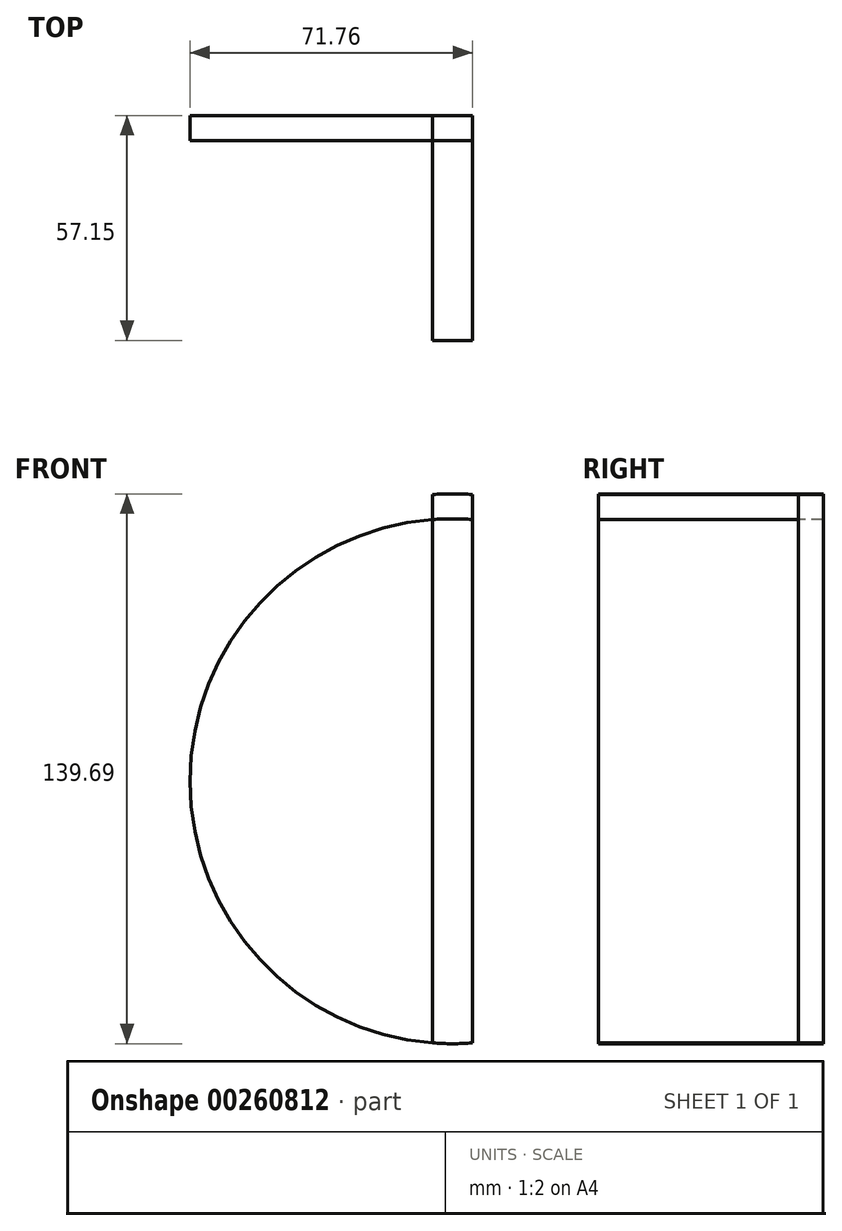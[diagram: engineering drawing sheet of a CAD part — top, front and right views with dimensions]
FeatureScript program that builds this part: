
annotation { "Feature Type Name" : "Feature", "Feature Type Description" : "" }
export const myFeature = defineFeature(function(context is Context, id is Id, definition is map)
    precondition{}
    {
        {
            var Q0;
            Q0=qCreatedBy(makeId("Front.planeOp"),FACE);
            var sketch = newSketch(context, id + "F0", { "sketchPlane" : qUnion([Q0])});
            skCircle(sketch, "E0", {"center": v(0, 0) * mm, "radius": 73.03 * mm});
            skPoint(sketch, "E1", {"position": v(-5.08, 0) * mm});
            skPoint(sketch, "E2.MirrorP", {"position": v(5.08, 0) * mm});
            skCircle(sketch, "E3", {"center": v(0, 0) * mm, "radius": 66.68 * mm});
            skLineSegment(sketch, "E4", {"start": v(-5.08, 0) * mm, "end": v(-5.08, 72.85) * mm});
            skLineSegment(sketch, "E5", {"start": v(-5.08, 72.85) * mm, "end": v(-5.08, -66.48) * mm});
            skLineSegment(sketch, "E6.MirrorCS", {"start": v(5.08, 72.85) * mm, "end": v(5.08, -66.48) * mm});
            skSolve(sketch);
        }
        {
            var Q0;
            {var subQ4=sQuery(id+"F0.wireOp",EDGE,"E5");var subQ7=sQuery(id+"F0.wireOp",EDGE,"E0");var subQ8=makeQuery(id+"F0.imprint","INTERSECT",VERTEX,{"derivedFrom":[subQ7,subQ4]});Q0=makeQuery(id+"F0.imprint","IMPRINT",FACE,{"disambiguationData":[TD([[makeQuery(id+"F0.imprint","IMPRINT",EDGE,{"disambiguationData":[TD([[subQ8,-1.0]])],"derivedFrom":subQ7}),1.0]])]});}
            var Q1;
            {var subQ0=sQuery(id+"F0.wireOp",EDGE,"E6.MirrorCS");var subQ1=sQuery(id+"F0.wireOp",EDGE,"E3");var subQ2=makeQuery(id+"F0.imprint","INTERSECT",VERTEX,{"disambiguationData":[OD(0.0)],"derivedFrom":[subQ1,subQ0]});Q1=makeQuery(id+"F0.imprint","IMPRINT",FACE,{"disambiguationData":[TD([[makeQuery(id+"F0.imprint","IMPRINT",EDGE,{"disambiguationData":[TD([[subQ2,-1.0]])],"derivedFrom":subQ1}),1.0]])]});}
            var Q2;
            {var subQ0=sQuery(id+"F0.wireOp",EDGE,"E5");var subQ1=sQuery(id+"F0.wireOp",EDGE,"E0");var subQ2=makeQuery(id+"F0.imprint","INTERSECT",VERTEX,{"derivedFrom":[subQ1,subQ0]});Q2=makeQuery(id+"F0.imprint","IMPRINT",FACE,{"disambiguationData":[TD([[makeQuery(id+"F0.imprint","IMPRINT",EDGE,{"disambiguationData":[TD([[subQ2,1.0]])],"derivedFrom":subQ1}),1.0]])]});}
            var Q3;
            {var subQ0=sQuery(id+"F0.wireOp",EDGE,"E5");var subQ4=makeQuery(id+"F0.imprint","IMPRINT",VERTEX,{"derivedFrom":subQ0});Q3=makeQuery(id+"F0.imprint","IMPRINT",FACE,{"disambiguationData":[TD([[makeQuery(id+"F0.imprint","IMPRINT",EDGE,{"disambiguationData":[TD([[subQ4,1.0]])],"derivedFrom":subQ0}),-1.0]])]});}
            var Q4;
            {var subQ0=sQuery(id+"F0.wireOp",EDGE,"E5");var subQ3=makeQuery(id+"F0.imprint","IMPRINT",VERTEX,{"derivedFrom":subQ0});Q4=makeQuery(id+"F0.imprint","IMPRINT",FACE,{"disambiguationData":[TD([[makeQuery(id+"F0.imprint","IMPRINT",EDGE,{"disambiguationData":[TD([[subQ3,1.0]])],"derivedFrom":subQ0}),1.0]])]});}
            extrude(context, id + "F1", {"entities" : qUnion([Q0, Q1, Q2, Q3, Q4]), "oppositeDirection" : true, "depth" : 6.35 * mm});
        }
        {
            var Q0;
            {var subQ4=sQuery(id+"F0.wireOp",EDGE,"E5");var subQ7=sQuery(id+"F0.wireOp",EDGE,"E0");var subQ8=makeQuery(id+"F0.imprint","INTERSECT",VERTEX,{"derivedFrom":[subQ7,subQ4]});Q0=makeQuery(id+"F0.imprint","IMPRINT",FACE,{"disambiguationData":[TD([[makeQuery(id+"F0.imprint","IMPRINT",EDGE,{"disambiguationData":[TD([[subQ8,-1.0]])],"derivedFrom":subQ7}),1.0]])]});}
            var Q1;
            {var subQ0=sQuery(id+"F0.wireOp",EDGE,"E5");var subQ1=sQuery(id+"F0.wireOp",EDGE,"E0");var subQ2=makeQuery(id+"F0.imprint","INTERSECT",VERTEX,{"derivedFrom":[subQ1,subQ0]});Q1=makeQuery(id+"F0.imprint","IMPRINT",FACE,{"disambiguationData":[TD([[makeQuery(id+"F0.imprint","IMPRINT",EDGE,{"disambiguationData":[TD([[subQ2,1.0]])],"derivedFrom":subQ1}),1.0]])]});}
            extrude(context, id + "F2", {"entities" : qUnion([Q0, Q1]), "depth" : 50.8 * mm});
        }
        {
            var Q0;
            {var subQ0=sQuery(id+"F0.wireOp",EDGE,"E5");var subQ3=makeQuery(id+"F0.imprint","IMPRINT",VERTEX,{"derivedFrom":subQ0});Q0=makeQuery(id+"F0.imprint","IMPRINT",FACE,{"disambiguationData":[TD([[makeQuery(id+"F0.imprint","IMPRINT",EDGE,{"disambiguationData":[TD([[subQ3,1.0]])],"derivedFrom":subQ0}),1.0]])]});}
            extrude(context, id + "F3", {"entities" : qUnion([Q0]), "depth" : 50.8 * mm});
        }
    });
